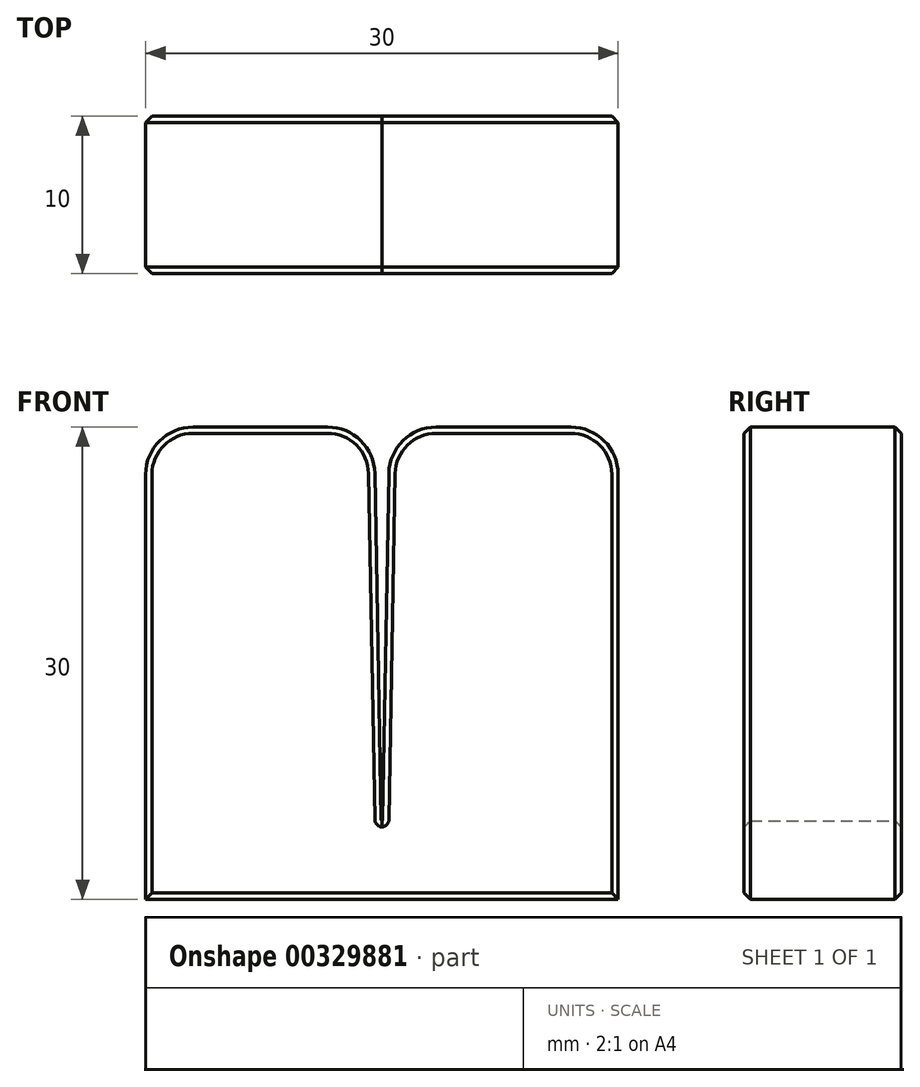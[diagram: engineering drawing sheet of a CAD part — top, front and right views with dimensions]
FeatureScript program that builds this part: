
annotation { "Feature Type Name" : "Feature", "Feature Type Description" : "" }
export const myFeature = defineFeature(function(context is Context, id is Id, definition is map)
    precondition{}
    {
        {
            var Q0;
            Q0=qCreatedBy(makeId("Front.planeOp"),FACE);
            var sketch = newSketch(context, id + "F0", { "sketchPlane" : qUnion([Q0])});
            skLineSegment(sketch, "E0", {"start": v(0, 0) * mm, "end": v(-15, 0) * mm});
            skLineSegment(sketch, "E1", {"start": v(-15, 0) * mm, "end": v(-15, 30) * mm});
            skLineSegment(sketch, "E2", {"start": v(-15, 30) * mm, "end": v(-0.5, 30) * mm});
            skLineSegment(sketch, "E3", {"start": v(0, 5) * mm, "end": v(0, 0) * mm, "construction": true});
            skLineSegment(sketch, "E4.MirrorCS", {"start": v(15, 30) * mm, "end": v(0.5, 30) * mm});
            skLineSegment(sketch, "E5.MirrorCS", {"start": v(15, 0) * mm, "end": v(15, 30) * mm});
            skLineSegment(sketch, "E6.MirrorCS", {"start": v(0, 0) * mm, "end": v(15, 0) * mm});
            skLineSegment(sketch, "E7", {"start": v(0.5, 30) * mm, "end": v(0.05, 5.09) * mm});
            skArc(sketch, "E8", {"start": v(0, 5) * mm, "mid": v(0.04, 5.04) * mm, "end": v(0.05, 5.09) * mm});
            skArc(sketch, "E9.MirrorCS", {"start": v(0, 5) * mm, "mid": v(-0.04, 5.04) * mm, "end": v(-0.05, 5.09) * mm});
            skLineSegment(sketch, "E10.MirrorCS", {"start": v(-0.5, 30) * mm, "end": v(-0.05, 5.09) * mm});
            skSolve(sketch);
        }
        {
            var Q0;
            Q0=makeQuery(id+"F0.imprint","IMPRINT",FACE,{"disambiguationData":[TD([[makeQuery(id+"F0.imprint","IMPRINT",EDGE,{"derivedFrom":sQuery(id+"F0.wireOp",EDGE,"E0")}),-1.0]])]});
            extrude(context, id + "F1", {"entities" : qUnion([Q0]), "depth" : 10 * mm, "offsetDistance" : 25 * mm});
        }
        {
            var Q0;
            Q0=makeQuery(id+"F1.opExtrude","SWEPT_EDGE",EDGE,{"disambiguationData":[OSD([sQuery(id+"F0.wireOp",EDGE,"E2"),sQuery(id+"F0.wireOp",EDGE,"unRYFiI1-gYfg-Au2u-oxmC-3FkZo5Bh0Zl3")])]});
            var Q1;
            Q1=makeQuery(id+"F1.opExtrude","SWEPT_EDGE",EDGE,{"disambiguationData":[OSD([sQuery(id+"F0.wireOp",EDGE,"fa90e10d-4bd7-484e-b44b-ed6ac15de0c80.MirrorCS"),sQuery(id+"F0.wireOp",EDGE,"E4.MirrorCS")])]});
            fillet(context, id + "F2", {"entities" : qUnion([Q0, Q1]), "tangentPropagation" : true, "radius" : 3 * mm, "defaultsChanged" : true, "vertexSettings" : [], "allowEdgeOverflow" : false});
        }
        {
            var Q0;
            Q0=makeQuery(id+"F1.opExtrude","CAP_FACE",FACE,{"disambiguationData":[OSD([sQuery(id+"F0.wireOp",EDGE,"E0"),sQuery(id+"F0.wireOp",EDGE,"E1"),sQuery(id+"F0.wireOp",EDGE,"E2"),sQuery(id+"F0.wireOp",EDGE,"unRYFiI1-gYfg-Au2u-oxmC-3FkZo5Bh0Zl3"),sQuery(id+"F0.wireOp",EDGE,"fa90e10d-4bd7-484e-b44b-ed6ac15de0c80.MirrorCS"),sQuery(id+"F0.wireOp",EDGE,"E4.MirrorCS"),sQuery(id+"F0.wireOp",EDGE,"E5.MirrorCS"),sQuery(id+"F0.wireOp",EDGE,"E6.MirrorCS")])],"isStart":false});
            var Q1;
            Q1=makeQuery(id+"F1.opExtrude","CAP_FACE",FACE,{"disambiguationData":[OSD([sQuery(id+"F0.wireOp",EDGE,"E0"),sQuery(id+"F0.wireOp",EDGE,"E1"),sQuery(id+"F0.wireOp",EDGE,"E2"),sQuery(id+"F0.wireOp",EDGE,"unRYFiI1-gYfg-Au2u-oxmC-3FkZo5Bh0Zl3"),sQuery(id+"F0.wireOp",EDGE,"fa90e10d-4bd7-484e-b44b-ed6ac15de0c80.MirrorCS"),sQuery(id+"F0.wireOp",EDGE,"E4.MirrorCS"),sQuery(id+"F0.wireOp",EDGE,"E5.MirrorCS"),sQuery(id+"F0.wireOp",EDGE,"E6.MirrorCS")])],"isStart":true});
            chamfer(context, id + "F3", {"entities" : qUnion([Q0, Q1]), "width" : 0.4 * mm, "tangentPropagation" : true});
        }
    });
